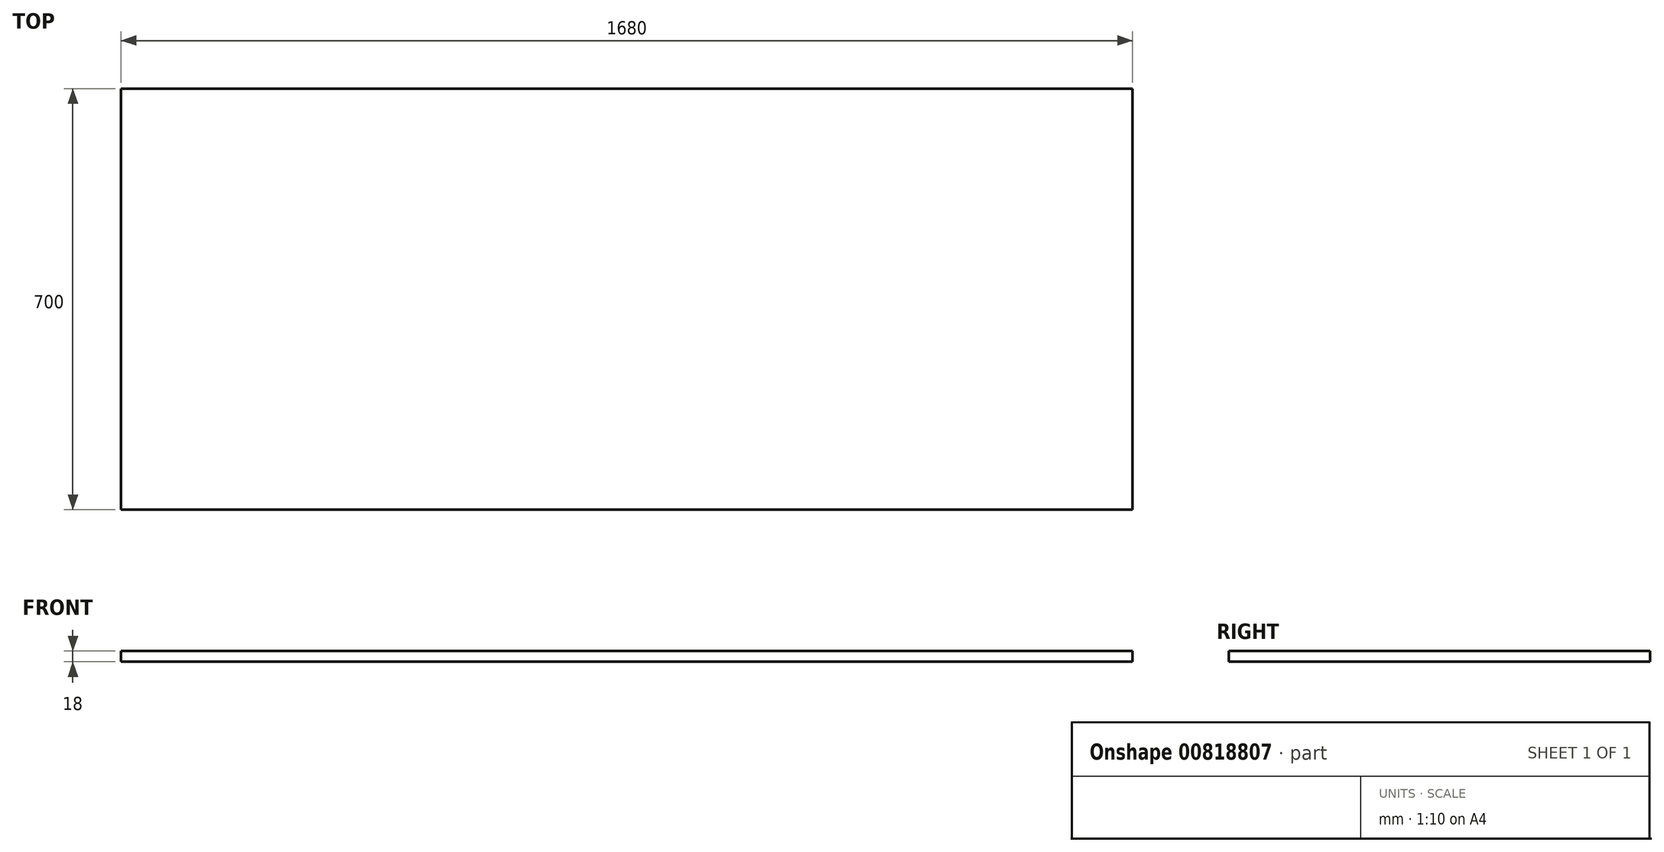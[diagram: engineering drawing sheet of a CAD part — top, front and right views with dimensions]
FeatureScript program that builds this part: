
annotation { "Feature Type Name" : "Feature", "Feature Type Description" : "" }
export const myFeature = defineFeature(function(context is Context, id is Id, definition is map)
    precondition{}
    {
        {
            var Q0;
            Q0=qCreatedBy(makeId("Top.planeOp"),FACE);
            var sketch = newSketch(context, id + "F0", { "sketchPlane" : qUnion([Q0])});
            skLineSegment(sketch, "E0.bottom", {"start": v(-840.14, 453.02) * mm, "end": v(839.86, 453.02) * mm});
            skLineSegment(sketch, "E0.top", {"start": v(-840.14, -246.98) * mm, "end": v(839.86, -246.98) * mm});
            skLineSegment(sketch, "E0.left", {"start": v(-840.14, 453.02) * mm, "end": v(-840.14, -246.98) * mm});
            skLineSegment(sketch, "E0.right", {"start": v(839.86, 453.02) * mm, "end": v(839.86, -246.98) * mm});
            skSolve(sketch);
        }
        {
            var Q0;
            Q0 = qSketchRegion(id + "F0", true);
            extrude(context, id + "F1", {"entities" : qUnion([Q0]), "depth" : 18 * mm, "offsetDistance" : 25 * mm});
        }
    });
